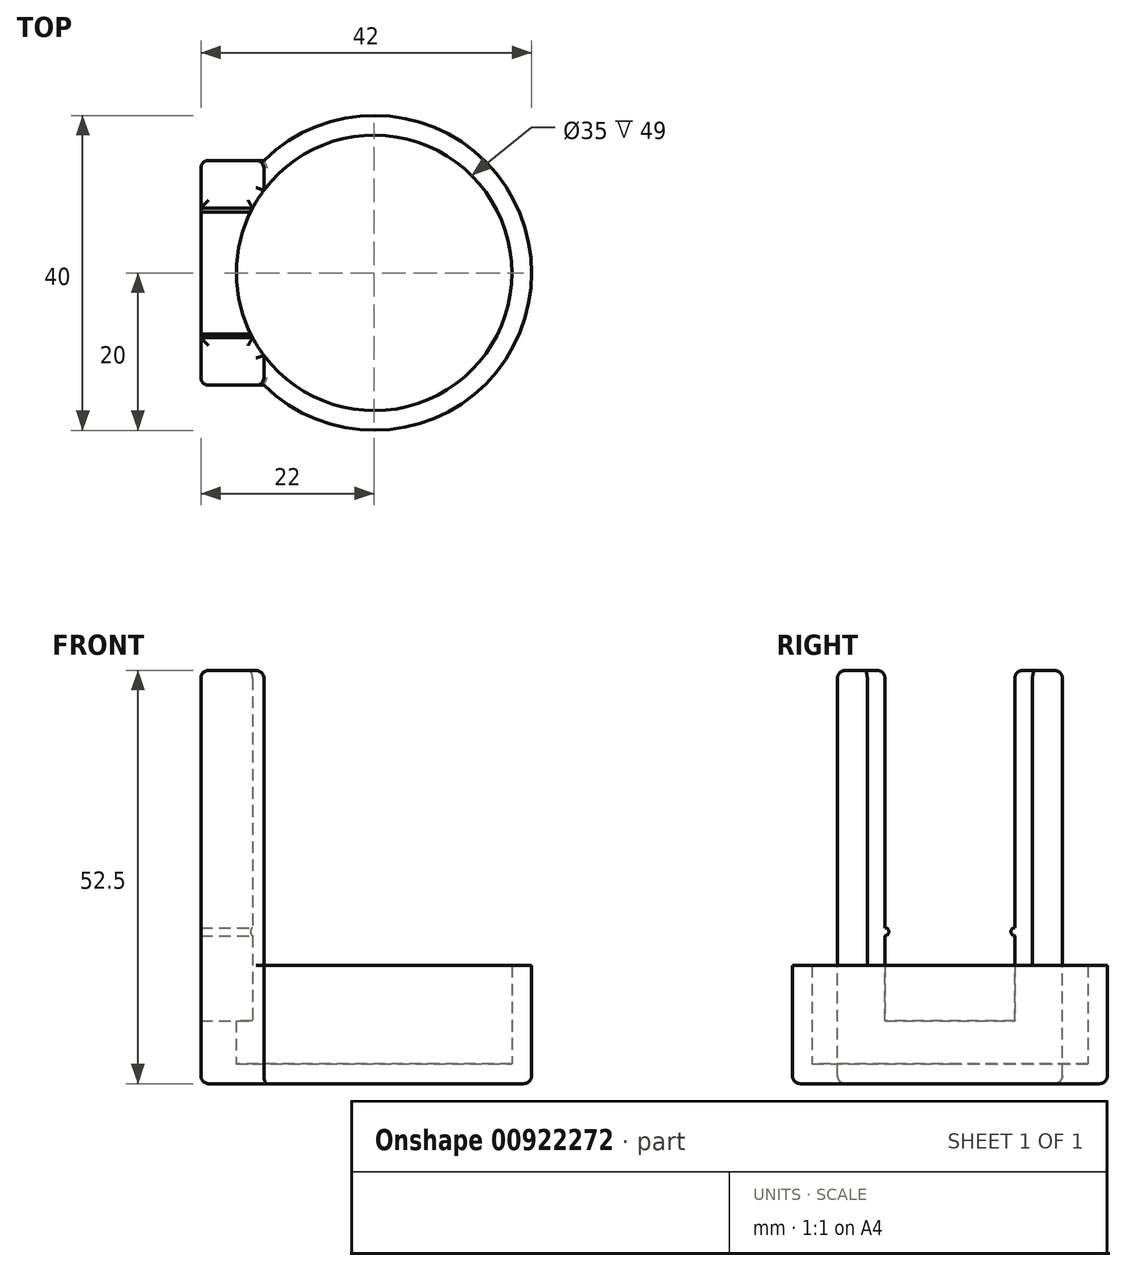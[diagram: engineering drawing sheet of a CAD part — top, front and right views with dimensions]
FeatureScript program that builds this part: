
annotation { "Feature Type Name" : "Feature", "Feature Type Description" : "" }
export const myFeature = defineFeature(function(context is Context, id is Id, definition is map)
    precondition{}
    {
        {
            var Q0;
            Q0=qCreatedBy(makeId("Top.planeOp"),FACE);
            var sketch = newSketch(context, id + "F0", { "sketchPlane" : qUnion([Q0])});
            skCircle(sketch, "E0", {"center": v(0, 0) * mm, "radius": 20 * mm});
            skSolve(sketch);
        }
        {
            var Q0;
            Q0 = qSketchRegion(id + "F0", true);
            extrude(context, id + "F1", {"entities" : qUnion([Q0]), "depth" : 50 * mm, "offsetDistance" : 25 * mm});
        }
        {
            var Q0;
            Q0=makeQuery(id+"F1.opExtrude","CAP_FACE",FACE,{"disambiguationData":[OSD([sQuery(id+"F0.wireOp",EDGE,"E0")])],"isStart":true});
            extrude(context, id + "F2", {"entities" : qUnion([Q0]), "operationType" : NewBodyOperationType.ADD, "depth" : 2.5 * mm, "offsetDistance" : 25 * mm});
        }
        {
            var Q0;
            Q0=qCreatedBy(makeId("Top.planeOp"),FACE);
            var sketch = newSketch(context, id + "F3", { "sketchPlane" : qUnion([Q0])});
            skCircle(sketch, "E1", {"center": v(0, 0) * mm, "radius": 17.5 * mm});
            skSolve(sketch);
        }
        {
            var Q0;
            Q0=qCreatedBy(makeId("Front.planeOp"),FACE);
            var sketch = newSketch(context, id + "F4", { "sketchPlane" : qUnion([Q0])});
            skLineSegment(sketch, "E2.bottom", {"start": v(26, 12.5) * mm, "end": v(-14, 12.5) * mm});
            skLineSegment(sketch, "E2.top", {"start": v(26, 62.5) * mm, "end": v(-14, 62.5) * mm});
            skLineSegment(sketch, "E2.left", {"start": v(26, 12.5) * mm, "end": v(26, 62.5) * mm});
            skLineSegment(sketch, "E2.right", {"start": v(-14, 12.5) * mm, "end": v(-14, 62.5) * mm});
            skSolve(sketch);
        }
        {
            var Q0;
            Q0 = qSketchRegion(id + "F4", true);
            extrude(context, id + "F5", {"entities" : qUnion([Q0]), "operationType" : NewBodyOperationType.REMOVE, "endBound" : BoundingType.SYMMETRIC, "depth" : 50 * mm, "offsetDistance" : 25 * mm});
        }
        {
            var Q0;
            Q0=qCreatedBy(makeId("Top.planeOp"),FACE);
            var sketch = newSketch(context, id + "F6", { "sketchPlane" : qUnion([Q0])});
            skLineSegment(sketch, "E3.bottom", {"start": v(-14, 14.28) * mm, "end": v(-22, 14.28) * mm});
            skLineSegment(sketch, "E3.top", {"start": v(-14, -14.28) * mm, "end": v(-22, -14.28) * mm});
            skLineSegment(sketch, "E3.left", {"start": v(-14, 14.28) * mm, "end": v(-14, -14.28) * mm});
            skLineSegment(sketch, "E3.right", {"start": v(-22, 14.28) * mm, "end": v(-22, -14.28) * mm});
            skSolve(sketch);
        }
        {
            var Q0;
            Q0 = qSketchRegion(id + "F6", true);
            extrude(context, id + "F7", {"entities" : qUnion([Q0]), "operationType" : NewBodyOperationType.ADD, "oppositeDirection" : true, "depth" : 2.5 * mm, "offsetDistance" : 25 * mm});
        }
        {
            var Q0;
            Q0 = qSketchRegion(id + "F6", true);
            extrude(context, id + "F8", {"entities" : qUnion([Q0]), "operationType" : NewBodyOperationType.ADD, "depth" : 50 * mm, "offsetDistance" : 25 * mm});
        }
        {
            var Q0;
            Q0 = qSketchRegion(id + "F3", true);
            extrude(context, id + "F9", {"entities" : qUnion([Q0]), "operationType" : NewBodyOperationType.REMOVE, "depth" : 50 * mm, "offsetDistance" : 25 * mm});
        }
        {
            var Q0;
            Q0=qCreatedBy(makeId("Right.planeOp"),FACE);
            var sketch = newSketch(context, id + "F10", { "sketchPlane" : qUnion([Q0])});
            skLineSegment(sketch, "E4.bottom", {"start": v(8.25, 50.5) * mm, "end": v(-8.25, 50.5) * mm});
            skLineSegment(sketch, "E4.top", {"start": v(8.25, 5.5) * mm, "end": v(-8.25, 5.5) * mm});
            skLineSegment(sketch, "E4.left", {"start": v(8.25, 50.5) * mm, "end": v(8.25, 5.5) * mm});
            skLineSegment(sketch, "E4.right", {"start": v(-8.25, 50.5) * mm, "end": v(-8.25, 5.5) * mm});
            skCircle(sketch, "E5", {"center": v(-8.25, 16.8) * mm, "radius": 0.5 * mm});
            skCircle(sketch, "E6", {"center": v(8.25, 16.8) * mm, "radius": 0.5 * mm});
            skSolve(sketch);
        }
        {
            var Q0;
            {var subQ4=sQuery(id+"F10.wireOp",EDGE,"E4.bottom");Q0=makeQuery(id+"F10.imprint","IMPRINT",FACE,{"disambiguationData":[TD([[makeQuery(id+"F10.imprint","IMPRINT",EDGE,{"derivedFrom":subQ4}),1.0]])]});}
            extrude(context, id + "F11", {"entities" : qUnion([Q0]), "operationType" : NewBodyOperationType.REMOVE, "oppositeDirection" : true, "depth" : 25 * mm, "offsetDistance" : 25 * mm});
        }
        {
            var Q0;
            Q0=makeQuery(id+"F7.boolean.opBoolean","MERGE",FACE,{"derivedFrom":[makeQuery(id+"F2.opExtrude","CAP_FACE",FACE,{"disambiguationData":[OSD([sQuery(id+"F0.wireOp",EDGE,"E0")])],"isStart":false}),makeQuery(id+"F7.opExtrude","CAP_FACE",FACE,{"disambiguationData":[OSD([sQuery(id+"F6.wireOp",EDGE,"E3.bottom"),sQuery(id+"F6.wireOp",EDGE,"E3.top"),sQuery(id+"F6.wireOp",EDGE,"E3.left"),sQuery(id+"F6.wireOp",EDGE,"E3.right")])],"isStart":false})]});
            var Q1;
            {var subQ0=sQuery(id+"F6.wireOp",EDGE,"E3.left");var subQ1=sQuery(id+"F6.wireOp",EDGE,"E3.top");Q1=makeQuery(id+"F8.boolean.opBoolean","MERGE",EDGE,{"derivedFrom":[makeQuery(id+"F7.opExtrude","SWEPT_EDGE",EDGE,{"disambiguationData":[OSD([subQ1,subQ0])]}),makeQuery(id+"F8.opExtrude","SWEPT_EDGE",EDGE,{"disambiguationData":[OSD([subQ1,subQ0])]})]});}
            var Q2;
            {var subQ0=sQuery(id+"F6.wireOp",EDGE,"E3.left");var subQ1=sQuery(id+"F6.wireOp",EDGE,"E3.bottom");Q2=makeQuery(id+"F8.boolean.opBoolean","MERGE",EDGE,{"derivedFrom":[makeQuery(id+"F7.opExtrude","SWEPT_EDGE",EDGE,{"disambiguationData":[OSD([subQ1,subQ0])]}),makeQuery(id+"F8.opExtrude","SWEPT_EDGE",EDGE,{"disambiguationData":[OSD([subQ1,subQ0])]})]});}
            var Q3;
            {var subQ0=sQuery(id+"F6.wireOp",EDGE,"E3.right");var subQ1=sQuery(id+"F6.wireOp",EDGE,"E3.bottom");Q3=makeQuery(id+"F8.boolean.opBoolean","MERGE",EDGE,{"derivedFrom":[makeQuery(id+"F7.opExtrude","SWEPT_EDGE",EDGE,{"disambiguationData":[OSD([subQ1,subQ0])]}),makeQuery(id+"F8.opExtrude","SWEPT_EDGE",EDGE,{"disambiguationData":[OSD([subQ1,subQ0])]})]});}
            var Q4;
            {var subQ0=sQuery(id+"F6.wireOp",EDGE,"E3.right");var subQ1=sQuery(id+"F6.wireOp",EDGE,"E3.top");Q4=makeQuery(id+"F8.boolean.opBoolean","MERGE",EDGE,{"derivedFrom":[makeQuery(id+"F7.opExtrude","SWEPT_EDGE",EDGE,{"disambiguationData":[OSD([subQ1,subQ0])]}),makeQuery(id+"F8.opExtrude","SWEPT_EDGE",EDGE,{"disambiguationData":[OSD([subQ1,subQ0])]})]});}
            var Q5;
            {var subQ0=sQuery(id+"F6.wireOp",EDGE,"E3.top");var subQ1=sQuery(id+"F6.wireOp",EDGE,"E3.right");Q5=makeQuery(id+"F11.boolean.opBoolean","SPLIT",FACE,{"disambiguationData":[TD([makeQuery(id+"F7.opExtrude","SWEPT_FACE",FACE,{"disambiguationData":[OSD([subQ0])]})])],"derivedFrom":makeQuery(id+"F8.boolean.opBoolean","MERGE",FACE,{"derivedFrom":[makeQuery(id+"F1.opExtrude","CAP_FACE",FACE,{"disambiguationData":[OSD([sQuery(id+"F0.wireOp",EDGE,"E0")])],"isStart":false}),makeQuery(id+"F8.opExtrude","CAP_FACE",FACE,{"disambiguationData":[OSD([sQuery(id+"F6.wireOp",EDGE,"E3.bottom"),subQ0,sQuery(id+"F6.wireOp",EDGE,"E3.left"),subQ1])],"isStart":false})]})});}
            var Q6;
            {var subQ0=sQuery(id+"F6.wireOp",EDGE,"E3.right");var subQ1=sQuery(id+"F6.wireOp",EDGE,"E3.bottom");Q6=makeQuery(id+"F11.boolean.opBoolean","SPLIT",FACE,{"disambiguationData":[TD([makeQuery(id+"F7.opExtrude","SWEPT_FACE",FACE,{"disambiguationData":[OSD([subQ1])]})])],"derivedFrom":makeQuery(id+"F8.boolean.opBoolean","MERGE",FACE,{"derivedFrom":[makeQuery(id+"F1.opExtrude","CAP_FACE",FACE,{"disambiguationData":[OSD([sQuery(id+"F0.wireOp",EDGE,"E0")])],"isStart":false}),makeQuery(id+"F8.opExtrude","CAP_FACE",FACE,{"disambiguationData":[OSD([subQ1,sQuery(id+"F6.wireOp",EDGE,"E3.top"),sQuery(id+"F6.wireOp",EDGE,"E3.left"),subQ0])],"isStart":false})]})});}
            fillet(context, id + "F12", {"entities" : qUnion([Q0, Q1, Q2, Q3, Q4, Q5, Q6]), "radius" : 1 * mm, "tangentPropagation" : true, "allowEdgeOverflow" : false});
        }
    });
